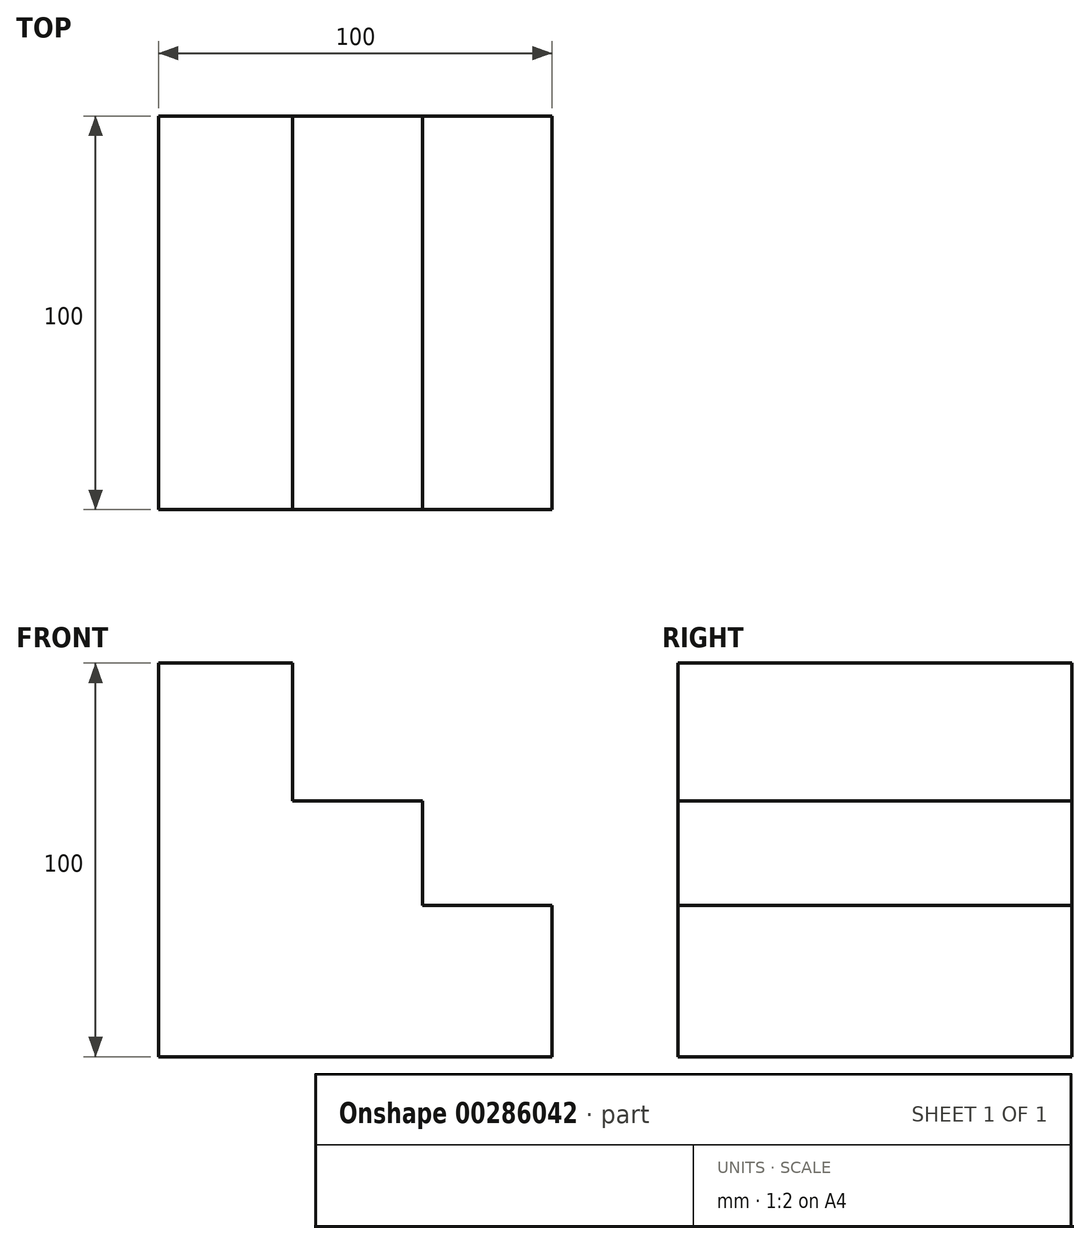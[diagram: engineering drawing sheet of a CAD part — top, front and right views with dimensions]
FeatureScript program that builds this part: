
annotation { "Feature Type Name" : "Feature", "Feature Type Description" : "" }
export const myFeature = defineFeature(function(context is Context, id is Id, definition is map)
    precondition{}
    {
        {
            var Q0;
            Q0=qCreatedBy(makeId("Top.planeOp"),FACE);
            var sketch = newSketch(context, id + "F0", { "sketchPlane" : qUnion([Q0])});
            skLineSegment(sketch, "E0.bottom", {"start": v(-50, -50) * mm, "end": v(50, -50) * mm});
            skLineSegment(sketch, "E0.top", {"start": v(-50, 50) * mm, "end": v(50, 50) * mm});
            skLineSegment(sketch, "E0.left", {"start": v(-50, -50) * mm, "end": v(-50, 50) * mm});
            skLineSegment(sketch, "E0.right", {"start": v(50, -50) * mm, "end": v(50, 50) * mm});
            skPoint(sketch, "E0.middle", {"position": v(0, 0) * mm});
            skSolve(sketch);
        }
        {
            var Q0;
            Q0=makeQuery(id+"F0.imprint","IMPRINT",FACE,{"disambiguationData":[TD([[makeQuery(id+"F0.imprint","IMPRINT",EDGE,{"derivedFrom":sQuery(id+"F0.wireOp",EDGE,"E0.bottom")}),1.0]])]});
            extrude(context, id + "F1", {"entities" : qUnion([Q0]), "depth" : 100 * mm});
        }
        {
            var Q0;
            Q0=makeQuery(id+"F1.opExtrude","SWEPT_FACE",FACE,{"disambiguationData":[OSD([sQuery(id+"F0.wireOp",EDGE,"E0.bottom")])]});
            var sketch = newSketch(context, id + "F2", { "sketchPlane" : qUnion([Q0])});
            skLineSegment(sketch, "E1", {"start": v(-16, 100) * mm, "end": v(-16, 64.91) * mm});
            skLineSegment(sketch, "E2", {"start": v(-16, 64.91) * mm, "end": v(17, 64.91) * mm});
            skLineSegment(sketch, "E3", {"start": v(17, 64.91) * mm, "end": v(17, 38.4) * mm});
            skLineSegment(sketch, "E4", {"start": v(17, 38.4) * mm, "end": v(50, 38.4) * mm});
            skSolve(sketch);
        }
        {
            var Q0;
            {var subQ1=sQuery(id+"F2.wireOp",EDGE,"E1");Q0=makeQuery(id+"F2.imprint","IMPRINT",FACE,{"disambiguationData":[TD([[makeQuery(id+"F2.imprint","IMPRINT",EDGE,{"derivedFrom":subQ1}),1.0]])]});}
            extrude(context, id + "F3", {"entities" : qUnion([Q0]), "operationType" : NewBodyOperationType.REMOVE, "oppositeDirection" : true, "depth" : 100 * mm});
        }
    });
